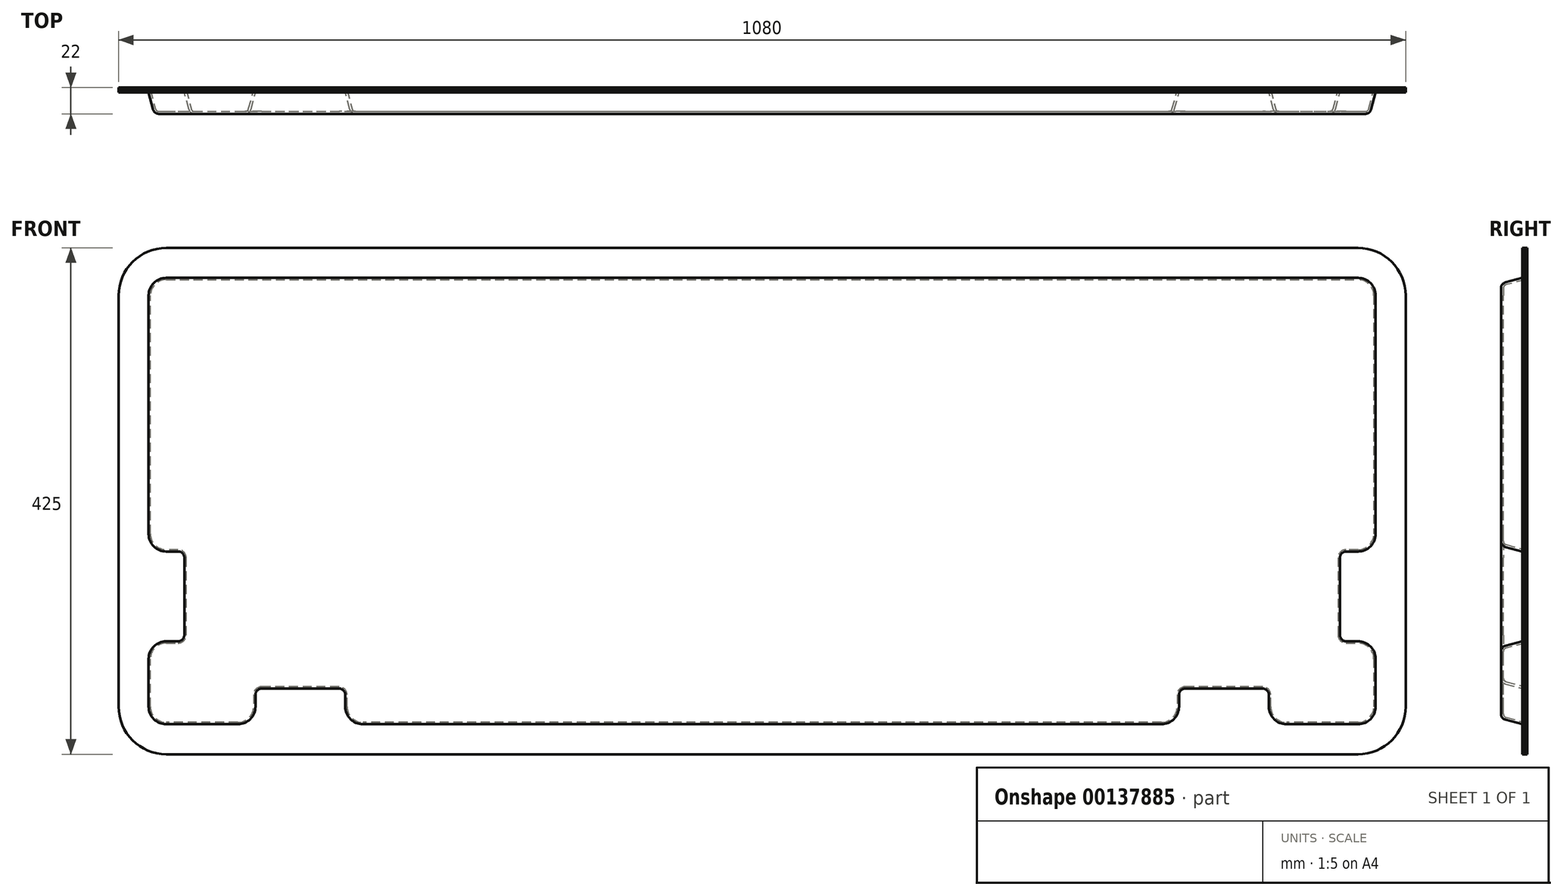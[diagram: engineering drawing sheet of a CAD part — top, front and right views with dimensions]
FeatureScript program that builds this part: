
annotation { "Feature Type Name" : "Feature", "Feature Type Description" : "" }
export const myFeature = defineFeature(function(context is Context, id is Id, definition is map)
    precondition{}
    {
        {
            var Q0;
            Q0=qCreatedBy(makeId("Front.planeOp"),FACE);
            var sketch = newSketch(context, id + "F0", { "sketchPlane" : qUnion([Q0])});
            skLineSegment(sketch, "E0.bottom", {"start": v(500, 212.5) * mm, "end": v(-500, 212.5) * mm});
            skLineSegment(sketch, "E0.top", {"start": v(500, -212.5) * mm, "end": v(-500, -212.5) * mm});
            skLineSegment(sketch, "E0.left", {"start": v(540, 172.5) * mm, "end": v(540, -172.5) * mm});
            skLineSegment(sketch, "E0.right", {"start": v(-540, 172.5) * mm, "end": v(-540, -172.5) * mm});
            skPoint(sketch, "E0.middle", {"position": v(0, 0) * mm});
            skPoint(sketch, "E1.visualSharp", {"position": v(-540, 212.5) * mm});
            skArc(sketch, "E1.filletArc", {"start": v(-500, 212.5) * mm, "mid": v(-528.28, 200.78) * mm, "end": v(-540, 172.5) * mm});
            skPoint(sketch, "E2.visualSharp", {"position": v(540, 212.5) * mm});
            skArc(sketch, "E2.filletArc", {"start": v(540, 172.5) * mm, "mid": v(528.28, 200.78) * mm, "end": v(500, 212.5) * mm});
            skPoint(sketch, "E3.visualSharp", {"position": v(540, -212.5) * mm});
            skArc(sketch, "E3.filletArc", {"start": v(500, -212.5) * mm, "mid": v(528.28, -200.78) * mm, "end": v(540, -172.5) * mm});
            skPoint(sketch, "E4.visualSharp", {"position": v(-540, -212.5) * mm});
            skArc(sketch, "E4.filletArc", {"start": v(-540, -172.5) * mm, "mid": v(-528.28, -200.78) * mm, "end": v(-500, -212.5) * mm});
            skArc(sketch, "E5.0", {"start": v(-500, 197.5) * mm, "mid": v(-517.68, 190.18) * mm, "end": v(-525, 172.5) * mm});
            skLineSegment(sketch, "E5.1", {"start": v(500, 197.5) * mm, "end": v(-500, 197.5) * mm});
            skLineSegment(sketch, "E5.2", {"start": v(-525, 172.5) * mm, "end": v(-525, -172.5) * mm});
            skArc(sketch, "E5.3", {"start": v(525, 172.5) * mm, "mid": v(517.68, 190.18) * mm, "end": v(500, 197.5) * mm});
            skArc(sketch, "E5.4", {"start": v(-525, -172.5) * mm, "mid": v(-517.68, -190.18) * mm, "end": v(-500, -197.5) * mm});
            skLineSegment(sketch, "E5.5", {"start": v(500, -197.5) * mm, "end": v(-500, -197.5) * mm});
            skArc(sketch, "E5.6", {"start": v(500, -197.5) * mm, "mid": v(517.68, -190.18) * mm, "end": v(525, -172.5) * mm});
            skLineSegment(sketch, "E5.7", {"start": v(525, 172.5) * mm, "end": v(525, -172.5) * mm});
            skSolve(sketch);
        }
        {
            var Q0;
            Q0=makeQuery(id+"F0.imprint","IMPRINT",FACE,{"disambiguationData":[TD([[makeQuery(id+"F0.imprint","IMPRINT",EDGE,{"derivedFrom":sQuery(id+"F0.wireOp",EDGE,"E5.0")}),1.0]])]});
            cPlane(context, id + "F1", {"entities" : qUnion([Q0]), "cplaneType" : CPlaneType.OFFSET, "offset" : 20 * mm, "width" : 150 * mm, "height" : 150 * mm});
        }
        {
            var Q0;
            Q0=qCreatedBy(id+"F1.planeOp",FACE);
            var sketch = newSketch(context, id + "F2", { "sketchPlane" : qUnion([Q0])});
            skArc(sketch, "E6.0", {"start": v(510, 172.5) * mm, "mid": v(507.07, 179.57) * mm, "end": v(500, 182.5) * mm});
            skLineSegment(sketch, "E6.2", {"start": v(500, 182.5) * mm, "end": v(-500, 182.5) * mm});
            skArc(sketch, "E6.3", {"start": v(500, -182.5) * mm, "mid": v(507.07, -179.57) * mm, "end": v(510, -172.5) * mm});
            skArc(sketch, "E6.4", {"start": v(-500, 182.5) * mm, "mid": v(-507.07, 179.57) * mm, "end": v(-510, 172.5) * mm});
            skLineSegment(sketch, "E6.5", {"start": v(-510, 172.5) * mm, "end": v(-510, -27.5) * mm});
            skArc(sketch, "E6.6", {"start": v(-510, -172.5) * mm, "mid": v(-507.07, -179.57) * mm, "end": v(-500, -182.5) * mm});
            skLineSegment(sketch, "E6.7", {"start": v(0, -182.5) * mm, "end": v(-335, -182.5) * mm});
            skLineSegment(sketch, "E7.bottom", {"start": v(-500, -37.5) * mm, "end": v(-490, -37.5) * mm});
            skLineSegment(sketch, "E7.top", {"start": v(-500, -122.5) * mm, "end": v(-490, -122.5) * mm});
            skLineSegment(sketch, "E7.right", {"start": v(-480, -47.5) * mm, "end": v(-480, -112.5) * mm});
            skLineSegment(sketch, "E8.top", {"start": v(-420, -152.5) * mm, "end": v(-355, -152.5) * mm});
            skLineSegment(sketch, "E8.left", {"start": v(-430, -172.5) * mm, "end": v(-430, -162.5) * mm});
            skLineSegment(sketch, "E8.right", {"start": v(-345, -172.5) * mm, "end": v(-345, -162.5) * mm});
            skLineSegment(sketch, "E9", {"start": v(0, 298.64) * mm, "end": v(0, -298.64) * mm, "construction": true});
            skPoint(sketch, "E10.visualSharp", {"position": v(-480, -37.5) * mm});
            skArc(sketch, "E10.filletArc", {"start": v(-480, -47.5) * mm, "mid": v(-482.93, -40.43) * mm, "end": v(-490, -37.5) * mm});
            skPoint(sketch, "E11.visualSharp", {"position": v(-480, -122.5) * mm});
            skArc(sketch, "E11.filletArc", {"start": v(-490, -122.5) * mm, "mid": v(-482.93, -119.57) * mm, "end": v(-480, -112.5) * mm});
            skPoint(sketch, "E12.visualSharp", {"position": v(-430, -152.5) * mm});
            skArc(sketch, "E12.filletArc", {"start": v(-420, -152.5) * mm, "mid": v(-427.07, -155.43) * mm, "end": v(-430, -162.5) * mm});
            skPoint(sketch, "E13.visualSharp", {"position": v(-345, -152.5) * mm});
            skArc(sketch, "E13.filletArc", {"start": v(-345, -162.5) * mm, "mid": v(-347.93, -155.43) * mm, "end": v(-355, -152.5) * mm});
            skLineSegment(sketch, "E14.trimOffspring", {"start": v(-510, -132.5) * mm, "end": v(-510, -172.5) * mm});
            skLineSegment(sketch, "E15.trimOffspring", {"start": v(-440, -182.5) * mm, "end": v(-500, -182.5) * mm});
            skPoint(sketch, "E16.visualSharp", {"position": v(-510, -37.5) * mm});
            skArc(sketch, "E16.filletArc", {"start": v(-510, -27.5) * mm, "mid": v(-507.07, -34.57) * mm, "end": v(-500, -37.5) * mm});
            skPoint(sketch, "E17.visualSharp", {"position": v(-510, -122.5) * mm});
            skArc(sketch, "E17.filletArc", {"start": v(-500, -122.5) * mm, "mid": v(-507.07, -125.43) * mm, "end": v(-510, -132.5) * mm});
            skPoint(sketch, "E18.visualSharp", {"position": v(-430, -182.5) * mm});
            skArc(sketch, "E18.filletArc", {"start": v(-440, -182.5) * mm, "mid": v(-432.93, -179.57) * mm, "end": v(-430, -172.5) * mm});
            skPoint(sketch, "E19.visualSharp", {"position": v(-345, -182.5) * mm});
            skArc(sketch, "E19.filletArc", {"start": v(-345, -172.5) * mm, "mid": v(-342.07, -179.57) * mm, "end": v(-335, -182.5) * mm});
            skArc(sketch, "E20.MirrorCS", {"start": v(510, -27.5) * mm, "mid": v(507.07, -34.57) * mm, "end": v(500, -37.5) * mm});
            skLineSegment(sketch, "E21.MirrorCS", {"start": v(500, -37.5) * mm, "end": v(490, -37.5) * mm});
            skArc(sketch, "E22.MirrorCS", {"start": v(480, -47.5) * mm, "mid": v(482.93, -40.43) * mm, "end": v(490, -37.5) * mm});
            skLineSegment(sketch, "E23.MirrorCS", {"start": v(480, -47.5) * mm, "end": v(480, -112.5) * mm});
            skArc(sketch, "E24.MirrorCS", {"start": v(490, -122.5) * mm, "mid": v(482.93, -119.57) * mm, "end": v(480, -112.5) * mm});
            skLineSegment(sketch, "E25.MirrorCS", {"start": v(500, -122.5) * mm, "end": v(490, -122.5) * mm});
            skArc(sketch, "E26.MirrorCS", {"start": v(500, -122.5) * mm, "mid": v(507.07, -125.43) * mm, "end": v(510, -132.5) * mm});
            skLineSegment(sketch, "E27.MirrorCS", {"start": v(510, -132.5) * mm, "end": v(510, -172.5) * mm});
            skLineSegment(sketch, "E28.MirrorCS", {"start": v(440, -182.5) * mm, "end": v(500, -182.5) * mm});
            skArc(sketch, "E29.MirrorCS", {"start": v(440, -182.5) * mm, "mid": v(432.93, -179.57) * mm, "end": v(430, -172.5) * mm});
            skLineSegment(sketch, "E30.MirrorCS", {"start": v(430, -172.5) * mm, "end": v(430, -162.5) * mm});
            skArc(sketch, "E31.MirrorCS", {"start": v(420, -152.5) * mm, "mid": v(427.07, -155.43) * mm, "end": v(430, -162.5) * mm});
            skLineSegment(sketch, "E32.MirrorCS", {"start": v(420, -152.5) * mm, "end": v(355, -152.5) * mm});
            skPoint(sketch, "E33.MirrorP", {"position": v(345, -152.5) * mm});
            skLineSegment(sketch, "E34.MirrorCS", {"start": v(345, -172.5) * mm, "end": v(345, -162.5) * mm});
            skArc(sketch, "E35.MirrorCS", {"start": v(345, -172.5) * mm, "mid": v(342.07, -179.57) * mm, "end": v(335, -182.5) * mm});
            skLineSegment(sketch, "E36.MirrorCS", {"start": v(0, -182.5) * mm, "end": v(335, -182.5) * mm});
            skArc(sketch, "E37.MirrorCS", {"start": v(345, -162.5) * mm, "mid": v(347.93, -155.43) * mm, "end": v(355, -152.5) * mm});
            skLineSegment(sketch, "E38.MirrorCS", {"start": v(510, 172.5) * mm, "end": v(510, -27.5) * mm});
            skSolve(sketch);
        }
        {
            var Q0;
            Q0=makeQuery(id+"F0.imprint","IMPRINT",FACE,{"disambiguationData":[TD([[makeQuery(id+"F0.imprint","IMPRINT",EDGE,{"derivedFrom":sQuery(id+"F0.wireOp",EDGE,"E0.bottom")}),1.0]])]});
            var Q1;
            Q1=makeQuery(id+"F0.imprint","IMPRINT",FACE,{"disambiguationData":[TD([[makeQuery(id+"F0.imprint","IMPRINT",EDGE,{"derivedFrom":sQuery(id+"F0.wireOp",EDGE,"E5.0")}),1.0]])]});
            extrude(context, id + "F3", {"entities" : qUnion([Q0, Q1]), "depth" : 2 * mm});
        }
        {
            var Q0;
            Q0=makeQuery(id+"F2.imprint","IMPRINT",FACE,{"disambiguationData":[TD([[makeQuery(id+"F2.imprint","IMPRINT",EDGE,{"derivedFrom":sQuery(id+"F2.wireOp",EDGE,"E6.0")}),1.0]])]});
            var Q1;
            Q1=makeQuery(id+"F3.opExtrude","CAP_FACE",FACE,{"disambiguationData":[OSD([sQuery(id+"F0.wireOp",EDGE,"E0.bottom"),sQuery(id+"F0.wireOp",EDGE,"E0.top"),sQuery(id+"F0.wireOp",EDGE,"E0.left"),sQuery(id+"F0.wireOp",EDGE,"E0.right"),sQuery(id+"F0.wireOp",EDGE,"E1.filletArc"),sQuery(id+"F0.wireOp",EDGE,"E2.filletArc"),sQuery(id+"F0.wireOp",EDGE,"E3.filletArc"),sQuery(id+"F0.wireOp",EDGE,"E4.filletArc")])],"isStart":false});
            extrude(context, id + "F4", {"entities" : qUnion([Q0]), "operationType" : NewBodyOperationType.ADD, "endBound" : BoundingType.UP_TO_SURFACE, "oppositeDirection" : true, "endBoundEntityFace" : qUnion([Q1]), "depth" : 25 * mm, "hasDraft" : true, "draftAngle" : 15 * degree});
        }
        {
            var Q0;
            Q0=makeQuery(id+"F4.opExtrude","CAP_FACE",FACE,{"disambiguationData":[OSD([sQuery(id+"F2.wireOp",EDGE,"E6.0"),sQuery(id+"F2.wireOp",EDGE,"E6.2"),sQuery(id+"F2.wireOp",EDGE,"E6.3"),sQuery(id+"F2.wireOp",EDGE,"E6.4"),sQuery(id+"F2.wireOp",EDGE,"E6.5"),sQuery(id+"F2.wireOp",EDGE,"E6.6"),sQuery(id+"F2.wireOp",EDGE,"E6.7"),sQuery(id+"F2.wireOp",EDGE,"E7.bottom"),sQuery(id+"F2.wireOp",EDGE,"E7.top"),sQuery(id+"F2.wireOp",EDGE,"E7.right"),sQuery(id+"F2.wireOp",EDGE,"E8.top"),sQuery(id+"F2.wireOp",EDGE,"E8.left"),sQuery(id+"F2.wireOp",EDGE,"E8.right"),sQuery(id+"F2.wireOp",EDGE,"E10.filletArc"),sQuery(id+"F2.wireOp",EDGE,"E11.filletArc"),sQuery(id+"F2.wireOp",EDGE,"E12.filletArc"),sQuery(id+"F2.wireOp",EDGE,"E13.filletArc"),sQuery(id+"F2.wireOp",EDGE,"E14.trimOffspring"),sQuery(id+"F2.wireOp",EDGE,"E15.trimOffspring"),sQuery(id+"F2.wireOp",EDGE,"E16.filletArc"),sQuery(id+"F2.wireOp",EDGE,"E17.filletArc"),sQuery(id+"F2.wireOp",EDGE,"E18.filletArc"),sQuery(id+"F2.wireOp",EDGE,"E19.filletArc"),sQuery(id+"F2.wireOp",EDGE,"E20.MirrorCS"),sQuery(id+"F2.wireOp",EDGE,"E21.MirrorCS"),sQuery(id+"F2.wireOp",EDGE,"E22.MirrorCS"),sQuery(id+"F2.wireOp",EDGE,"E23.MirrorCS"),sQuery(id+"F2.wireOp",EDGE,"E24.MirrorCS"),sQuery(id+"F2.wireOp",EDGE,"E25.MirrorCS"),sQuery(id+"F2.wireOp",EDGE,"E26.MirrorCS"),sQuery(id+"F2.wireOp",EDGE,"E27.MirrorCS"),sQuery(id+"F2.wireOp",EDGE,"E28.MirrorCS"),sQuery(id+"F2.wireOp",EDGE,"E29.MirrorCS"),sQuery(id+"F2.wireOp",EDGE,"E30.MirrorCS"),sQuery(id+"F2.wireOp",EDGE,"E31.MirrorCS"),sQuery(id+"F2.wireOp",EDGE,"E32.MirrorCS"),sQuery(id+"F2.wireOp",EDGE,"E34.MirrorCS"),sQuery(id+"F2.wireOp",EDGE,"E35.MirrorCS"),sQuery(id+"F2.wireOp",EDGE,"E36.MirrorCS"),sQuery(id+"F2.wireOp",EDGE,"E37.MirrorCS"),sQuery(id+"F2.wireOp",EDGE,"E38.MirrorCS")])],"isStart":true});
            var Q1;
            Q1=makeQuery(id+"F4.opExtrude","CAP_EDGE",EDGE,{"disambiguationData":[OSD([sQuery(id+"F2.wireOp",EDGE,"E6.7"),sQuery(id+"F2.wireOp",EDGE,"E36.MirrorCS")])],"isStart":false});
            fillet(context, id + "F5", {"entities" : qUnion([Q0, Q1]), "radius" : 5 * mm, "tangentPropagation" : true, "allowEdgeOverflow" : false});
        }
        {
            var Q0;
            Q0=makeQuery(id+"F3.opExtrude","CAP_FACE",FACE,{"disambiguationData":[OSD([sQuery(id+"F0.wireOp",EDGE,"E0.bottom"),sQuery(id+"F0.wireOp",EDGE,"E0.top"),sQuery(id+"F0.wireOp",EDGE,"E0.left"),sQuery(id+"F0.wireOp",EDGE,"E0.right"),sQuery(id+"F0.wireOp",EDGE,"E1.filletArc"),sQuery(id+"F0.wireOp",EDGE,"E2.filletArc"),sQuery(id+"F0.wireOp",EDGE,"E3.filletArc"),sQuery(id+"F0.wireOp",EDGE,"E4.filletArc")])],"isStart":true});
            shell(context, id + "F6", {"entities" : qUnion([Q0]), "thickness" : 2 * mm});
        }
        {
            var Q0;
            Q0=makeQuery(id+"F0.imprint","IMPRINT",FACE,{"disambiguationData":[TD([[makeQuery(id+"F0.imprint","IMPRINT",EDGE,{"derivedFrom":sQuery(id+"F0.wireOp",EDGE,"E0.bottom")}),1.0]])]});
            var Q1;
            Q1=makeQuery(id+"F0.imprint","IMPRINT",FACE,{"disambiguationData":[TD([[makeQuery(id+"F0.imprint","IMPRINT",EDGE,{"derivedFrom":sQuery(id+"F0.wireOp",EDGE,"E5.0")}),1.0]])]});
            extrude(context, id + "F7", {"entities" : qUnion([Q0, Q1]), "oppositeDirection" : true, "depth" : 2 * mm});
        }
    });
